# Revit family: Gira_103900
name_source: partatom
category: Electrical Fixtures
revit_build: Autodesk Revit 2017 (Build: 20160225_1515(x64)
units: mm (PartAtom-declared; Revit-internal decimal feet)

## family parameters
Cut with Voids When Loaded = No
Host = Face
Maintain Annotation Orientation = No
Part Type = Normal
Room Calculation Point = No
Round Connector Dimension = Use Diameter
Shared = No

## types (1)
- Blind act. 4-g AC 230 V man.act. KNX DRA
    BIM = https://media.live.bim.site 8f.rfa
    BIMSITE_PRODUCT_ID = 5731a3003bfc5e22ed9e73e750135267efe85297
    Bus connection included = No
    Cost = 0 $
    Default Elevation = 1219 mm
    Description = Blind act.4g AC 230V DRA KNX KNX blind actuator, 4-gang AC 230 V   DC 12 - 48 V with manual actuation,DRA plus Blind actuators with integrated bus coupler, manual activation, and status display for each output. For controlling electrically operated blinds, shutters, awnings, ventilation flaps, or similar hangings.,Features: - Curtain position can be directly controlled. - Slat position can be directly controlled. - Behaviour after bus voltage failure and recovery can be set. - Separately parameterisable movement times with movement time extension for moving into the upper end position. - Central control of all blind outputs possible. - Feedback of the curtain position or slat position. - Feedback can be delayed until after the recovery of bus voltage. - Assignments of up to five different safety functions (three wind alarms, one rain alarm, one frost alarm) or optionally with cyclical monitoring. - Forced setting function can be realised for each blind output. - Integration in scenes is possible, 8 internal scenes at the most can be parameterised per channel. - Memory function for light scenes. - Sun protection function with fixed and variable curtain or slat positions can be activated. - Extended sun protection with extensive control functions. - Integration in temperature management of building possible. - Blocking of individual outputs manually or with bus. - Active or passive (object can be read out) cyclical feedback functions. - Building site operation: Outputs can be operated manually without bus voltage with operating voltage only. - For mains voltage AC 230 V (4 channel) or low voltage DC 12 to 48 V (2 channel). - Connection of various external conductors. - Independent control of the four blind outputs. - Automatic curtain moving time detection for AC 230 V drives with mechanical stop position switches.,Notes : - Installation on DIN top-hat rail. - VDE approval in accordance with EN 60669-1, EN 60669-2-1.
    GTIN = 4010337042211
    HAN = 103900
    HeinzeBIM = https://www.heinze.de
    Local operation/hand operation = Yes
    Manufacturer = Gira
    Max. number of venetian-blind outputs = 4
    Number of binary inputs = 0
    Number of inputs = 1
    Number of outputs = 0
    Suitable for C-load = No
    URL = https://www.gira.de
    With switch function = No

## geometry (parser evidence)
native form markers: Blend x2, Sweep x3
no freeform markers — native parametric forms only
